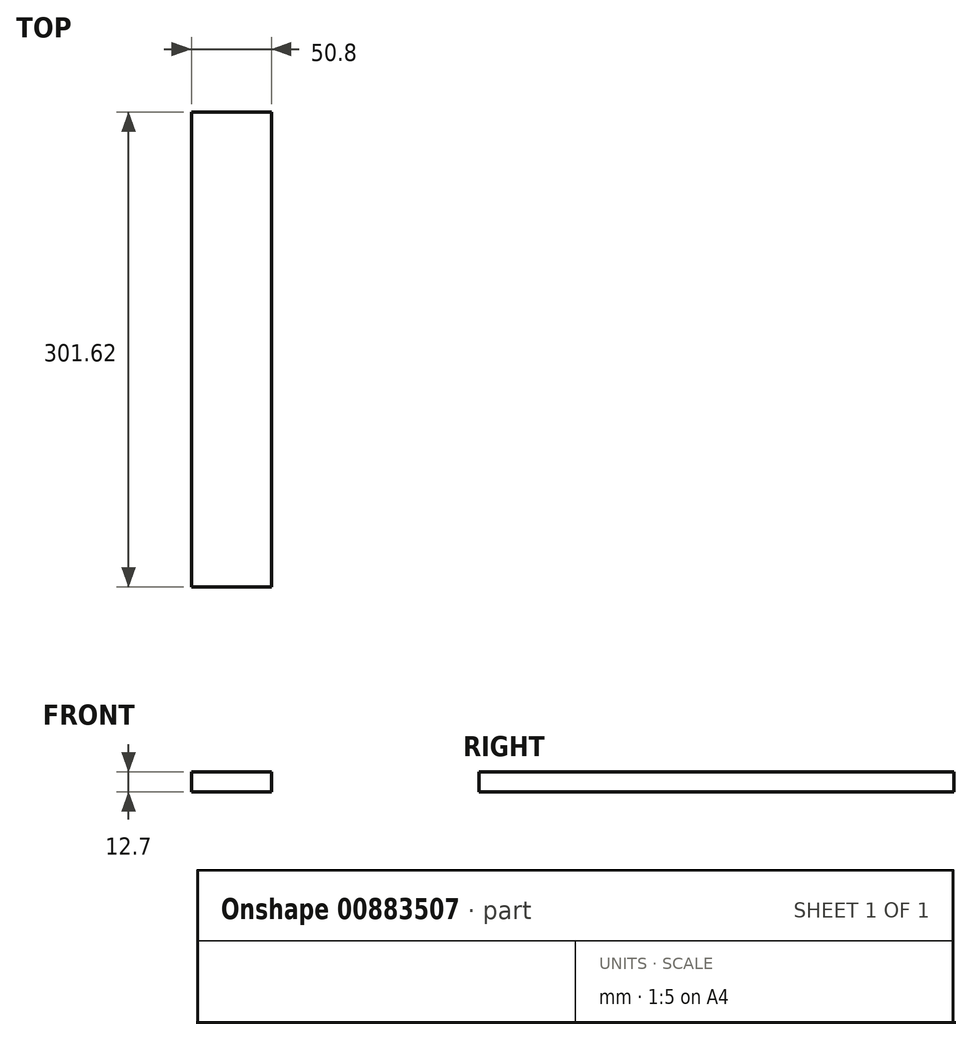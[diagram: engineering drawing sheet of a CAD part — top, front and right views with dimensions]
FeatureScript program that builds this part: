
annotation { "Feature Type Name" : "Feature", "Feature Type Description" : "" }
export const myFeature = defineFeature(function(context is Context, id is Id, definition is map)
    precondition{}
    {
        {
            var Q0;
            Q0=qCreatedBy(makeId("Front.planeOp"),FACE);
            var sketch = newSketch(context, id + "F0", { "sketchPlane" : qUnion([Q0])});
            skLineSegment(sketch, "E0.bottom", {"start": v(0, 0) * mm, "end": v(50.8, 0) * mm});
            skLineSegment(sketch, "E0.top", {"start": v(0, 12.7) * mm, "end": v(50.8, 12.7) * mm});
            skLineSegment(sketch, "E0.left", {"start": v(0, 0) * mm, "end": v(0, 12.7) * mm});
            skLineSegment(sketch, "E0.right", {"start": v(50.8, 0) * mm, "end": v(50.8, 12.7) * mm});
            skSolve(sketch);
        }
        {
            var Q0;
            Q0=qSketchRegion(id+"F0",true);
            extrude(context, id + "F1", {"entities" : qUnion([Q0]), "oppositeDirection" : true, "depth" : 301.62 * mm, "offsetDistance" : 25.4 * mm});
        }
    });
